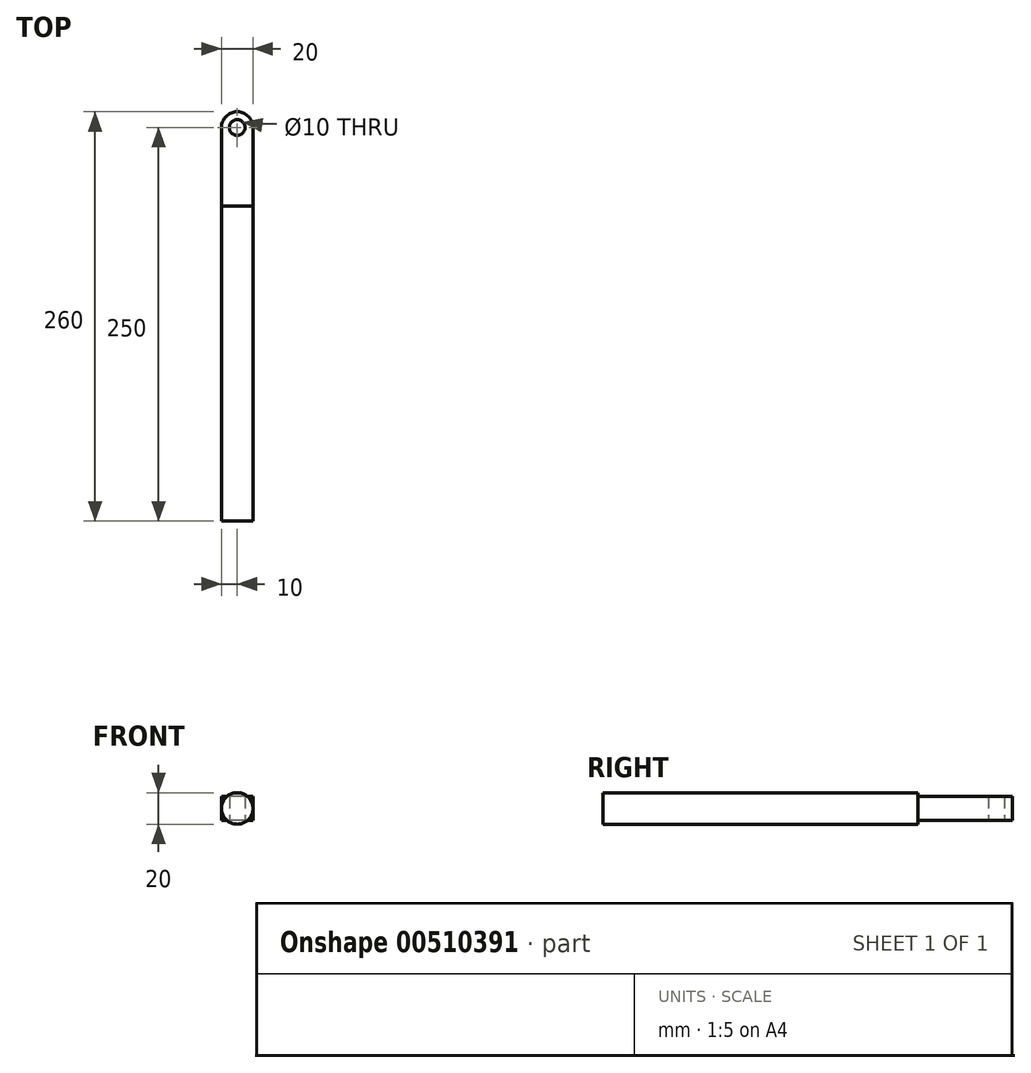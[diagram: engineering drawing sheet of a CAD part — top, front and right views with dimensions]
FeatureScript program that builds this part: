
annotation { "Feature Type Name" : "Feature", "Feature Type Description" : "" }
export const myFeature = defineFeature(function(context is Context, id is Id, definition is map)
    precondition{}
    {
        {
            var Q0;
            Q0=qCreatedBy(makeId("Top.planeOp"),FACE);
            var sketch = newSketch(context, id + "F0", { "sketchPlane" : qUnion([Q0])});
            skLineSegment(sketch, "E0.top", {"start": v(10, -25) * mm, "end": v(-10, -25) * mm});
            skLineSegment(sketch, "E0.left", {"start": v(10, 25) * mm, "end": v(10, -25) * mm});
            skLineSegment(sketch, "E0.right", {"start": v(-10, 25) * mm, "end": v(-10, -25) * mm});
            skPoint(sketch, "E0.middle", {"position": v(0, 0) * mm});
            skArc(sketch, "E1", {"start": v(10, 25) * mm, "mid": v(0, 35) * mm, "end": v(-10, 25) * mm});
            skCircle(sketch, "E2", {"center": v(0, 25) * mm, "radius": 5 * mm});
            skSolve(sketch);
        }
        {
            var Q0;
            Q0=makeQuery(id+"F0.imprint","IMPRINT",FACE,{"disambiguationData":[TD([[makeQuery(id+"F0.imprint","IMPRINT",EDGE,{"derivedFrom":sQuery(id+"F0.wireOp",EDGE,"E0.top")}),-1.0]])]});
            extrude(context, id + "F1", {"entities" : qUnion([Q0]), "endBound" : BoundingType.SYMMETRIC, "depth" : 15 * mm});
        }
        {
            var Q0;
            Q0=makeQuery(id+"F1.opExtrude","SWEPT_FACE",FACE,{"disambiguationData":[OSD([sQuery(id+"F0.wireOp",EDGE,"E0.top")])]});
            var sketch = newSketch(context, id + "F2", { "sketchPlane" : qUnion([Q0])});
            skCircle(sketch, "E3", {"center": v(0, 0) * mm, "radius": 10 * mm});
            skSolve(sketch);
        }
        {
            var Q0;
            Q0 = qSketchRegion(id + "F2", true);
            extrude(context, id + "F3", {"entities" : qUnion([Q0]), "operationType" : NewBodyOperationType.ADD, "depth" : 200 * mm});
        }
    });
